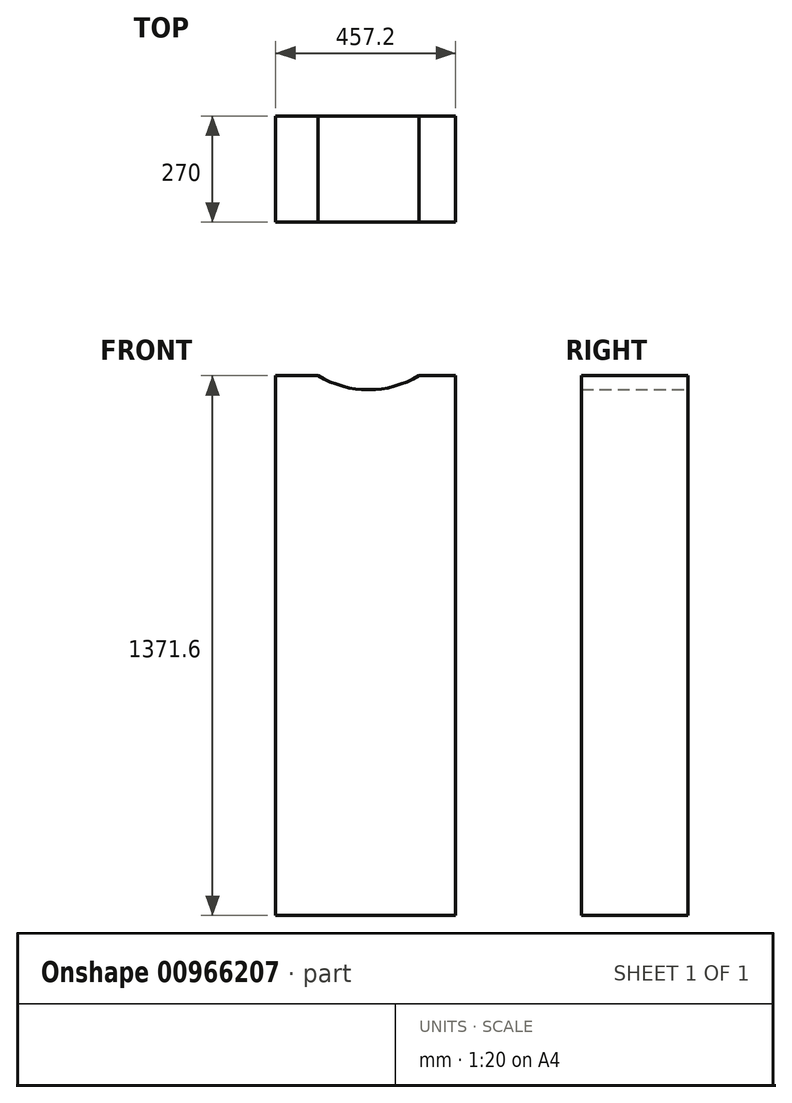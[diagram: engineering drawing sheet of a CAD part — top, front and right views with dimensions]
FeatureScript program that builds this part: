
annotation { "Feature Type Name" : "Feature", "Feature Type Description" : "" }
export const myFeature = defineFeature(function(context is Context, id is Id, definition is map)
    precondition{}
    {
        {
            var Q0;
            Q0=qCreatedBy(makeId("Front.planeOp"),FACE);
            var sketch = newSketch(context, id + "F0", { "sketchPlane" : qUnion([Q0])});
            skLineSegment(sketch, "E0.bottom", {"start": v(0, 0) * mm, "end": v(-457.2, 0) * mm});
            skLineSegment(sketch, "E0.top", {"start": v(0, 1371.6) * mm, "end": v(-457.2, 1371.6) * mm});
            skLineSegment(sketch, "E0.left", {"start": v(0, 0) * mm, "end": v(0, 1371.6) * mm});
            skLineSegment(sketch, "E0.right", {"start": v(-457.2, 0) * mm, "end": v(-457.2, 1371.6) * mm});
            skCircle(sketch, "E1", {"center": v(-221.2, 1582.83) * mm, "radius": 246.93 * mm});
            skPoint(sketch, "E2", {"position": v(-199.44, 1828.8) * mm});
            skSolve(sketch);
        }
        {
            var Q0;
            {var subQ0=sQuery(id+"F0.wireOp",EDGE,"E1");var subQ1=sQuery(id+"F0.wireOp",EDGE,"E0.top");var subQ2=makeQuery(id+"F0.imprint","INTERSECT",VERTEX,{"disambiguationData":[OD(0.0)],"derivedFrom":[subQ1,subQ0]});Q0=makeQuery(id+"F0.imprint","IMPRINT",FACE,{"disambiguationData":[TD([[makeQuery(id+"F0.imprint","IMPRINT",EDGE,{"disambiguationData":[TD([[subQ2,-1.0]])],"derivedFrom":subQ1}),-1.0]])]});}
            var Q1;
            Q1=makeQuery(id+"F0.imprint","IMPRINT",FACE,{"disambiguationData":[TD([[makeQuery(id+"F0.imprint","IMPRINT",EDGE,{"derivedFrom":sQuery(id+"F0.wireOp",EDGE,"E0.bottom")}),-1.0]])]});
            var Q2;
            {var subQ0=sQuery(id+"F0.wireOp",EDGE,"E1");var subQ1=sQuery(id+"F0.wireOp",EDGE,"E0.top");var subQ2=makeQuery(id+"F0.imprint","INTERSECT",VERTEX,{"disambiguationData":[OD(0.0)],"derivedFrom":[subQ1,subQ0]});Q2=makeQuery(id+"F0.imprint","IMPRINT",FACE,{"disambiguationData":[TD([[makeQuery(id+"F0.imprint","IMPRINT",EDGE,{"disambiguationData":[TD([[subQ2,-1.0]])],"derivedFrom":subQ1}),1.0]])]});}
            extrude(context, id + "F1", {"entities" : qUnion([Q0, Q1, Q2]), "depth" : 270 * mm, "offsetDistance" : 25 * mm});
        }
    });
